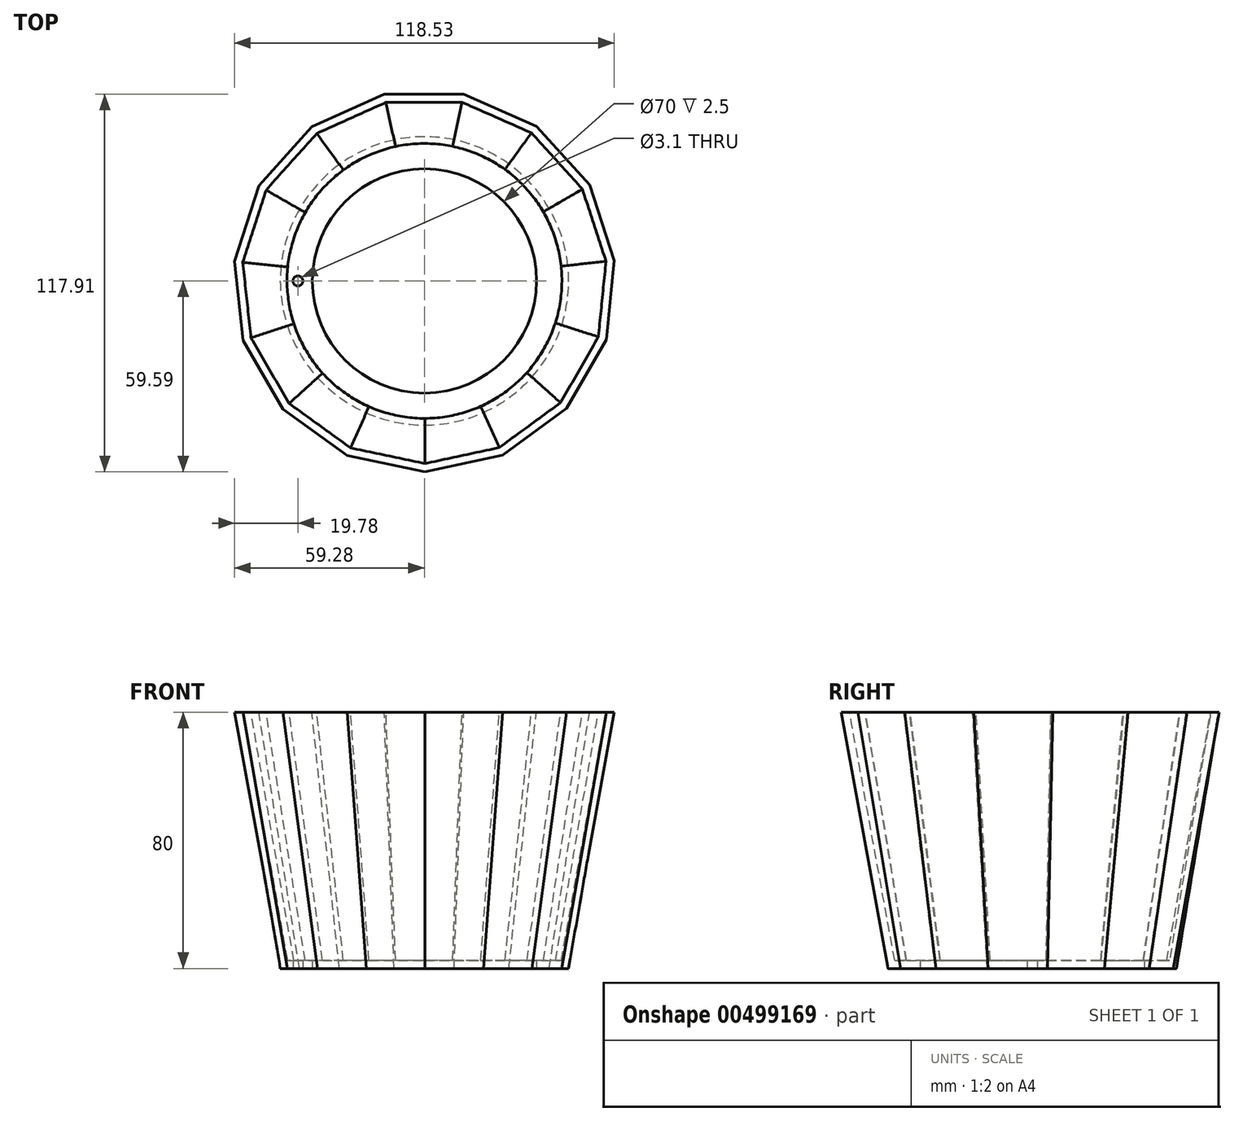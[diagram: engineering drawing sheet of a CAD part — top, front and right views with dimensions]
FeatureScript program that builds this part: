
annotation { "Feature Type Name" : "Feature", "Feature Type Description" : "" }
export const myFeature = defineFeature(function(context is Context, id is Id, definition is map)
    precondition{}
    {
        {
            var Q0;
            Q0=qCreatedBy(makeId("Top.planeOp"),FACE);
            var sketch = newSketch(context, id + "F0", { "sketchPlane" : qUnion([Q0])});
            skCircle(sketch, "E0", {"center": v(0, 0) * mm, "radius": 45 * mm});
            skSolve(sketch);
        }
        {
            var Q0;
            Q0=qCreatedBy(makeId("Front.planeOp"),FACE);
            var sketch = newSketch(context, id + "F1", { "sketchPlane" : qUnion([Q0])});
            skLineSegment(sketch, "E1", {"start": v(0, -67.38) * mm, "end": v(0, 70.35) * mm, "construction": true});
            skSolve(sketch);
        }
        {
            var Q0;
            Q0=qCreatedBy(makeId("Top.planeOp"),FACE);
            cPlane(context, id + "F2", {"entities" : qUnion([Q0]), "cplaneType" : CPlaneType.OFFSET, "offset" : 80 * mm, "width" : 150 * mm, "height" : 150 * mm});
        }
        {
            var Q0;
            Q0=qCreatedBy(id+"F2.planeOp",FACE);
            var sketch = newSketch(context, id + "F3", { "sketchPlane" : qUnion([Q0])});
            skCircle(sketch, "E2.cCircle", {"center": v(0, 0) * mm, "radius": 59.6 * mm, "construction": true});
            skLineSegment(sketch, "E2.0", {"start": v(59.25, 6.4) * mm, "end": v(56.73, -18.25) * mm});
            skLineSegment(sketch, "E2.1", {"start": v(56.73, -18.25) * mm, "end": v(44.4, -39.75) * mm});
            skLineSegment(sketch, "E2.2", {"start": v(44.4, -39.75) * mm, "end": v(24.4, -54.37) * mm});
            skLineSegment(sketch, "E2.3", {"start": v(24.4, -54.37) * mm, "end": v(0.17, -59.6) * mm});
            skLineSegment(sketch, "E2.4", {"start": v(0.17, -59.6) * mm, "end": v(-24.08, -54.5) * mm});
            skLineSegment(sketch, "E2.5", {"start": v(-24.08, -54.5) * mm, "end": v(-44.17, -40) * mm});
            skLineSegment(sketch, "E2.6", {"start": v(-44.17, -40) * mm, "end": v(-56.62, -18.58) * mm});
            skLineSegment(sketch, "E2.7", {"start": v(-56.62, -18.58) * mm, "end": v(-59.28, 6.06) * mm});
            skLineSegment(sketch, "E2.8", {"start": v(-59.28, 6.06) * mm, "end": v(-51.7, 29.65) * mm});
            skLineSegment(sketch, "E2.9", {"start": v(-51.7, 29.65) * mm, "end": v(-35.16, 48.11) * mm});
            skLineSegment(sketch, "E2.10", {"start": v(-35.16, 48.11) * mm, "end": v(-12.56, 58.25) * mm});
            skLineSegment(sketch, "E2.11", {"start": v(-12.56, 58.25) * mm, "end": v(12.22, 58.32) * mm});
            skLineSegment(sketch, "E2.12", {"start": v(12.22, 58.32) * mm, "end": v(34.89, 48.31) * mm});
            skLineSegment(sketch, "E2.13", {"start": v(34.89, 48.31) * mm, "end": v(51.52, 29.94) * mm});
            skLineSegment(sketch, "E2.14", {"start": v(51.52, 29.94) * mm, "end": v(59.25, 6.4) * mm});
            skSolve(sketch);
        }
        {
            var Q0;
            Q0=makeQuery(id+"F0.imprint","IMPRINT",FACE,{"disambiguationData":[TD([[makeQuery(id+"F0.imprint","IMPRINT",EDGE,{"derivedFrom":sQuery(id+"F0.wireOp",EDGE,"E0")}),1.0]])]});
            var Q1;
            Q1=makeQuery(id+"F3.imprint","IMPRINT",FACE,{"disambiguationData":[TD([[makeQuery(id+"F3.imprint","IMPRINT",EDGE,{"derivedFrom":sQuery(id+"F3.wireOp",EDGE,"E2.0")}),-1.0]])]});
            loft(context, id + "F4", {"sheetProfilesArray" : [{ "sheetProfileEntities" : qUnion([Q0]) }, { "sheetProfileEntities" : qUnion([Q1]) }]});
        }
        {
            var Q0;
            Q0=makeQuery(id+"F4.opLoft","CAP_FACE",FACE,{"disambiguationData":[OSD([makeQuery(id+"F3.imprint","IMPRINT",FACE,{"disambiguationData":[TD([[makeQuery(id+"F3.imprint","IMPRINT",EDGE,{"derivedFrom":sQuery(id+"F3.wireOp",EDGE,"E2.0")}),-1.0]])]})])],"isStart":true});
            shell(context, id + "F5", {"entities" : qUnion([Q0]), "thickness" : 2.5 * mm});
        }
        {
            var Q0;
            Q0=makeQuery(id+"F0.imprint","IMPRINT",FACE,{"disambiguationData":[TD([[makeQuery(id+"F0.imprint","IMPRINT",EDGE,{"derivedFrom":sQuery(id+"F0.wireOp",EDGE,"E0")}),1.0]])]});
            var sketch = newSketch(context, id + "F6", { "sketchPlane" : qUnion([Q0])});
            skCircle(sketch, "E3", {"center": v(0, 0) * mm, "radius": 35 * mm});
            skSolve(sketch);
        }
        {
            var Q0;
            Q0 = qSketchRegion(id + "F6", true);
            extrude(context, id + "F7", {"entities" : qUnion([Q0]), "operationType" : NewBodyOperationType.REMOVE, "depth" : 5 * mm});
        }
        {
            var Q0;
            Q0=qCreatedBy(makeId("Top.planeOp"),FACE);
            var sketch = newSketch(context, id + "F8", { "sketchPlane" : qUnion([Q0])});
            skCircle(sketch, "E4", {"center": v(-39.5, 0) * mm, "radius": 1.55 * mm});
            skSolve(sketch);
        }
        {
            var Q0;
            Q0=makeQuery(id+"F8.imprint","IMPRINT",FACE,{"disambiguationData":[TD([[makeQuery(id+"F8.imprint","IMPRINT",EDGE,{"derivedFrom":sQuery(id+"F8.wireOp",EDGE,"E4")}),1.0]])]});
            extrude(context, id + "F9", {"entities" : qUnion([Q0]), "operationType" : NewBodyOperationType.REMOVE, "depth" : 5 * mm});
        }
    });
